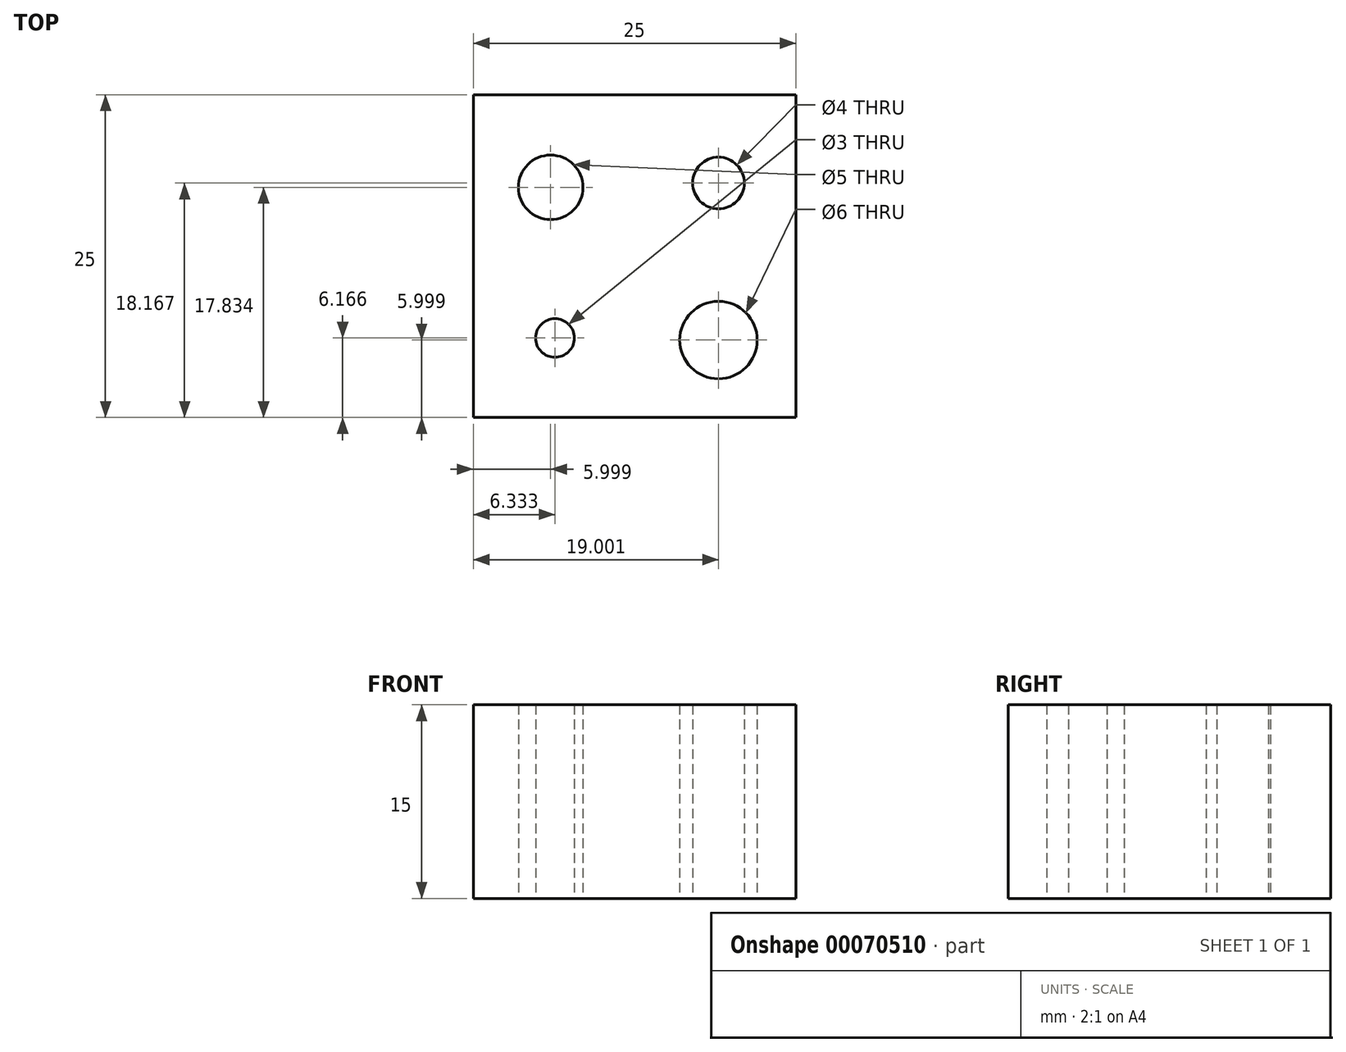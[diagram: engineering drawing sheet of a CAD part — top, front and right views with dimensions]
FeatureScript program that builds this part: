
annotation { "Feature Type Name" : "Feature", "Feature Type Description" : "" }
export const myFeature = defineFeature(function(context is Context, id is Id, definition is map)
    precondition{}
    {
        {
            var Q0;
            Q0=qCreatedBy(makeId("Top.planeOp"),FACE);
            var sketch = newSketch(context, id + "F0", { "sketchPlane" : qUnion([Q0])});
            skLineSegment(sketch, "E0.rect.bottom", {"start": v(12.5, 12.5) * mm, "end": v(-12.5, 12.5) * mm});
            skLineSegment(sketch, "E0.rect.top", {"start": v(12.5, -12.5) * mm, "end": v(-12.5, -12.5) * mm});
            skLineSegment(sketch, "E0.rect.left", {"start": v(12.5, 12.5) * mm, "end": v(12.5, -12.5) * mm});
            skLineSegment(sketch, "E0.rect.right", {"start": v(-12.5, 12.5) * mm, "end": v(-12.5, -12.5) * mm});
            skPoint(sketch, "E0.rect.middle", {"position": v(0, 0) * mm});
            skCircle(sketch, "E1", {"center": v(-6.5, 5.33) * mm, "radius": 2.5 * mm});
            skCircle(sketch, "E2", {"center": v(-6.17, -6.33) * mm, "radius": 1.5 * mm});
            skCircle(sketch, "E3", {"center": v(6.5, 5.67) * mm, "radius": 2 * mm});
            skCircle(sketch, "E4", {"center": v(6.5, -6.5) * mm, "radius": 3 * mm});
            skSolve(sketch);
        }
        {
            var Q0;
            Q0=makeQuery(id+"F0.imprint","IMPRINT",FACE,{"disambiguationData":[TD([[makeQuery(id+"F0.imprint","IMPRINT",EDGE,{"derivedFrom":sQuery(id+"F0.wireOp",EDGE,"E0.rect.bottom")}),1.0]])]});
            extrude(context, id + "F1", {"entities" : qUnion([Q0]), "depth" : 15 * mm});
        }
    });
